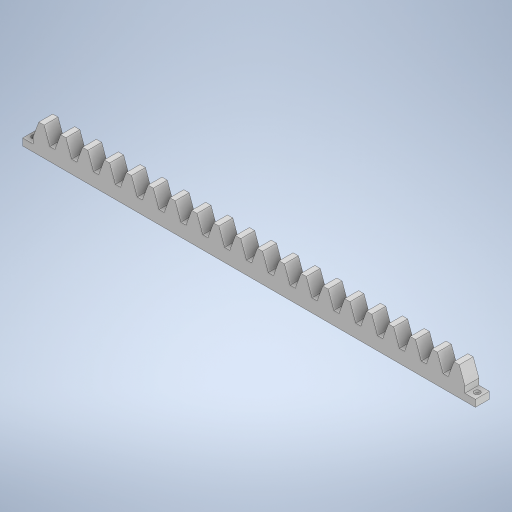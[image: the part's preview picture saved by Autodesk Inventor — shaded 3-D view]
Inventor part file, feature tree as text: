
AUTODESK INVENTOR PART (.ipt)
format: ipt  version: 2023.2 (Build 272271030, 271C)  size: 442,368 bytes
history: native  units: mm
features: projected_geometry x6, extrude x4, sketch x4
ambient origin geometry x8: Origin, YZ Plane, XZ Plane, XY Plane, X Axis, Y Axis, Z Axis, Center Point
bodies: Solid1 (feature_tree)
feature tree (14):
  extrude  "Extrusion1"  Depth=12.217305mm
  extrude  "Extrusion2"  Depth=10.0mm
  extrude  "Extrusion3"  Depth=18.862928mm
  extrude  "Extrusion4"  Depth=3.5mm
  sketch  "Sketch1"  dims[d3=30.0mm d4=12.217305mm]
  sketch  "Sketch2"  dims[d5=14.91mm d6=200.0mm d8=31.41mm d9=10.0mm d11=10.0mm]
  projected_geometry  "Projected Loop1"
  projected_geometry  "Projected Loop2"
  sketch  "Sketch3"  dims[d13=18.862928mm d14=620.799256mm d15=18.862928mm]
  projected_geometry  "Projected Loop3"
  projected_geometry  "Projected Loop4"
  sketch  "Sketch4"  dims[d16=18.862928mm d18=13.17215mm d19=13.17215mm d20=24.009256mm d21=22.5mm d22=23.944mm d23=3.010685mm d24=18.862928mm d25=20.0mm d26=0.0mm d27=15.0mm d28=20.0mm d29=15.0mm d30=20.0mm d31=10.0mm d32=0.0mm d33=5.3mm d34=0.0mm d35=0.0mm d36=8.7mm d37=3.5mm d38=0.0mm]
  projected_geometry  "Projected Loop5"
  projected_geometry  "Projected Loop6"
